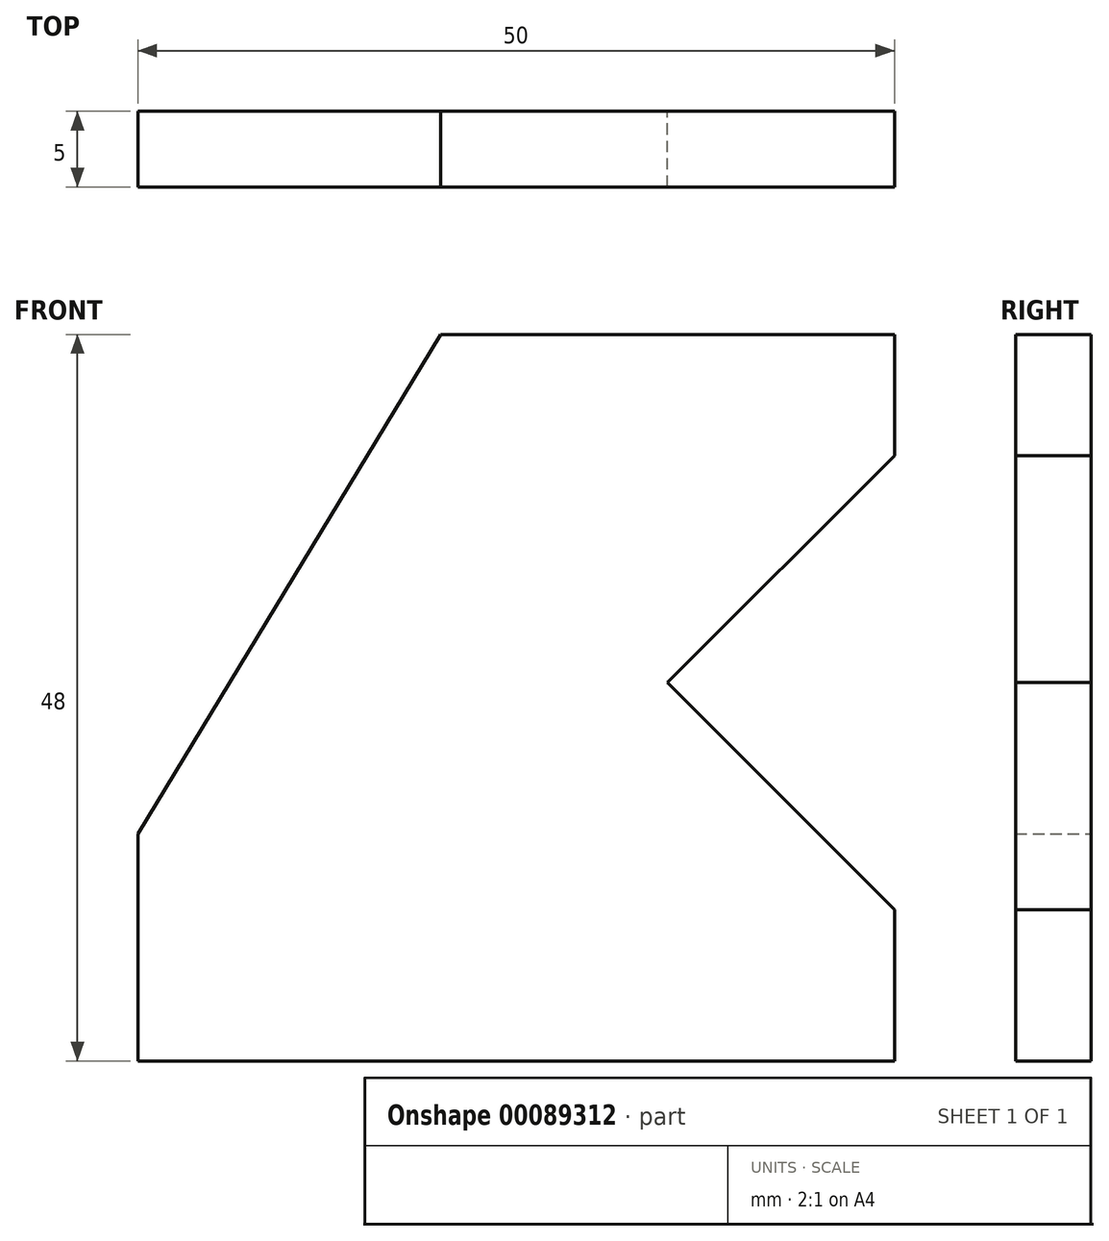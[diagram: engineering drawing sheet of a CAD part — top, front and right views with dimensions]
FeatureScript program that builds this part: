
annotation { "Feature Type Name" : "Feature", "Feature Type Description" : "" }
export const myFeature = defineFeature(function(context is Context, id is Id, definition is map)
    precondition{}
    {
        {
            var Q0;
            Q0=qCreatedBy(makeId("Front.planeOp"),FACE);
            var sketch = newSketch(context, id + "F0", { "sketchPlane" : qUnion([Q0])});
            skLineSegment(sketch, "E0", {"start": v(0, 0) * mm, "end": v(15, -15) * mm});
            skLineSegment(sketch, "E1", {"start": v(15, -25) * mm, "end": v(-35, -25) * mm});
            skLineSegment(sketch, "E2", {"start": v(-35, -25) * mm, "end": v(-35, -10) * mm});
            skLineSegment(sketch, "E3", {"start": v(-35, -10) * mm, "end": v(-15, 23) * mm});
            skLineSegment(sketch, "E4", {"start": v(-15, 23) * mm, "end": v(15, 23) * mm});
            skLineSegment(sketch, "E5", {"start": v(15, 15) * mm, "end": v(0, 0) * mm});
            skLineSegment(sketch, "E6", {"start": v(15, -25) * mm, "end": v(15, -15) * mm});
            skLineSegment(sketch, "E7.trimOffspring", {"start": v(15, 15) * mm, "end": v(15, 23) * mm});
            skSolve(sketch);
        }
        {
            var Q0;
            Q0 = qSketchRegion(id + "F0", true);
            extrude(context, id + "F1", {"entities" : qUnion([Q0]), "depth" : 5 * mm});
        }
    });
